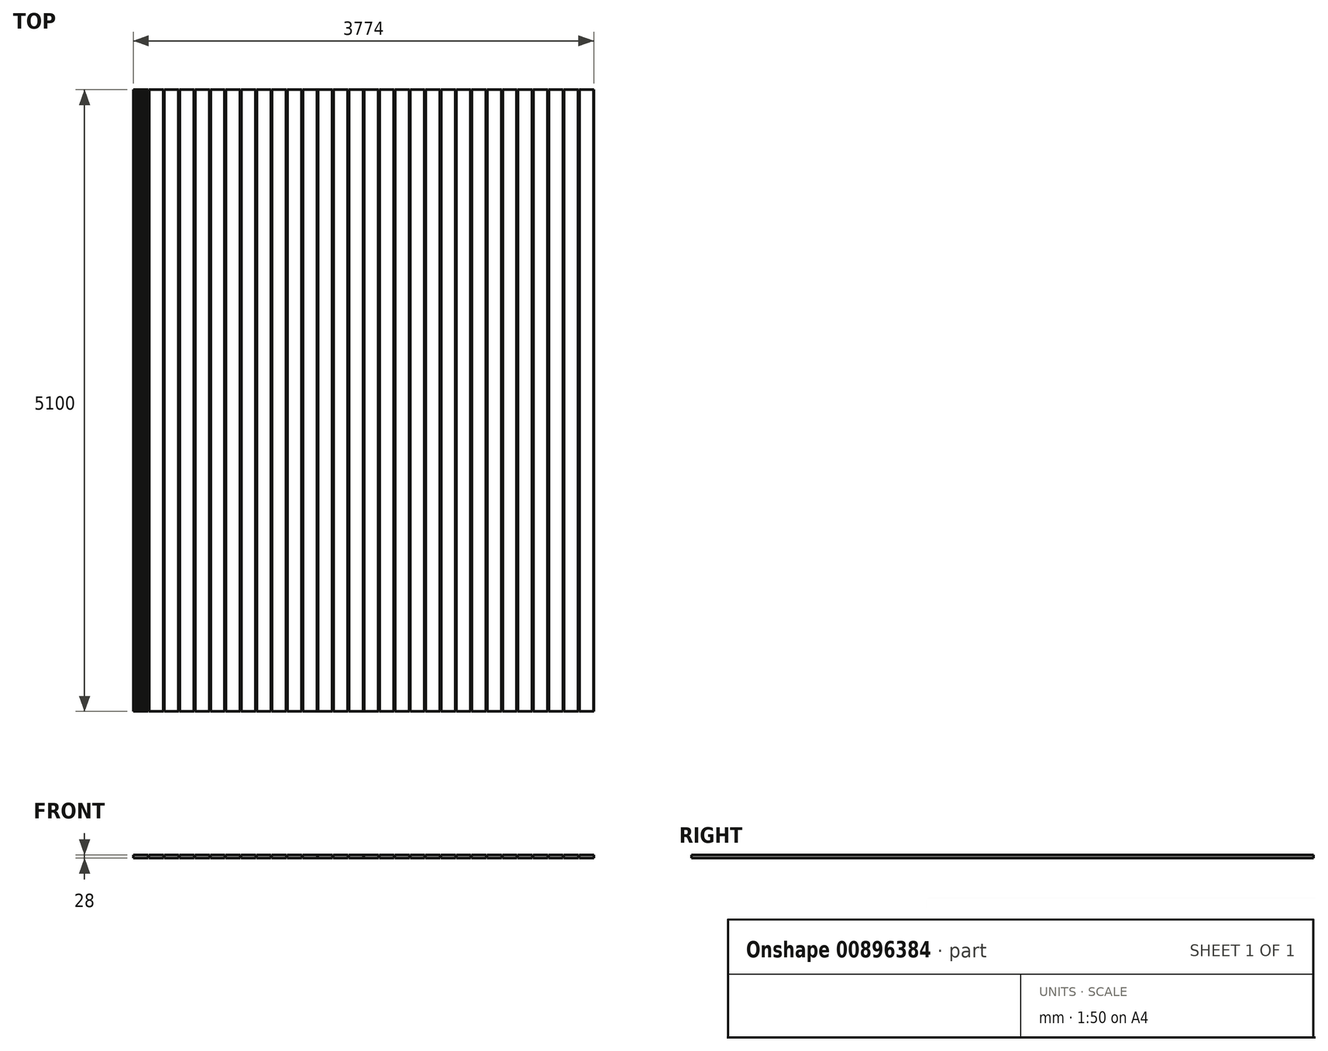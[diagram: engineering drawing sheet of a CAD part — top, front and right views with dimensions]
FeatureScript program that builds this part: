
annotation { "Feature Type Name" : "Feature", "Feature Type Description" : "" }
export const myFeature = defineFeature(function(context is Context, id is Id, definition is map)
    precondition{}
    {
        {
            var Q0;
            Q0=qCreatedBy(makeId("Top.planeOp"),FACE);
            var sketch = newSketch(context, id + "F0", { "sketchPlane" : qUnion([Q0])});
            skLineSegment(sketch, "E0.bottom", {"start": v(-61.1, -252.6) * mm, "end": v(58.9, -252.6) * mm});
            skLineSegment(sketch, "E0.top", {"start": v(-61.1, 4847.4) * mm, "end": v(58.9, 4847.4) * mm});
            skLineSegment(sketch, "E0.left", {"start": v(-61.1, -252.6) * mm, "end": v(-61.1, 4847.4) * mm});
            skLineSegment(sketch, "E0.right", {"start": v(58.9, -252.6) * mm, "end": v(58.9, 4847.4) * mm});
            skLineSegment(sketch, "E1.bottom", {"start": v(64.9, -252.6) * mm, "end": v(184.9, -252.6) * mm});
            skLineSegment(sketch, "E1.top", {"start": v(64.9, 4847.4) * mm, "end": v(184.9, 4847.4) * mm});
            skLineSegment(sketch, "E1.left", {"start": v(64.9, -252.6) * mm, "end": v(64.9, 4847.4) * mm});
            skLineSegment(sketch, "E1.right", {"start": v(184.9, -252.6) * mm, "end": v(184.9, 4847.4) * mm});
            skLineSegment(sketch, "E2.bottom", {"start": v(190.9, -252.6) * mm, "end": v(310.9, -252.6) * mm});
            skLineSegment(sketch, "E2.top", {"start": v(190.9, 4847.4) * mm, "end": v(310.9, 4847.4) * mm});
            skLineSegment(sketch, "E2.left", {"start": v(190.9, -252.6) * mm, "end": v(190.9, 4847.4) * mm});
            skLineSegment(sketch, "E2.right", {"start": v(310.9, -252.6) * mm, "end": v(310.9, 4847.4) * mm});
            skLineSegment(sketch, "E3.bottom", {"start": v(316.9, -252.6) * mm, "end": v(436.9, -252.6) * mm});
            skLineSegment(sketch, "E3.top", {"start": v(316.9, 4847.4) * mm, "end": v(436.9, 4847.4) * mm});
            skLineSegment(sketch, "E3.left", {"start": v(316.9, -252.6) * mm, "end": v(316.9, 4847.4) * mm});
            skLineSegment(sketch, "E3.right", {"start": v(436.9, -252.6) * mm, "end": v(436.9, 4847.4) * mm});
            skLineSegment(sketch, "E4.bottom", {"start": v(442.9, -252.6) * mm, "end": v(562.9, -252.6) * mm});
            skLineSegment(sketch, "E4.top", {"start": v(442.9, 4847.4) * mm, "end": v(562.9, 4847.4) * mm});
            skLineSegment(sketch, "E4.left", {"start": v(442.9, -252.6) * mm, "end": v(442.9, 4847.4) * mm});
            skLineSegment(sketch, "E4.right", {"start": v(562.9, -252.6) * mm, "end": v(562.9, 4847.4) * mm});
            skLineSegment(sketch, "E5.bottom", {"start": v(568.9, -252.6) * mm, "end": v(688.9, -252.6) * mm});
            skLineSegment(sketch, "E5.top", {"start": v(568.9, 4847.4) * mm, "end": v(688.9, 4847.4) * mm});
            skLineSegment(sketch, "E5.left", {"start": v(568.9, -252.6) * mm, "end": v(568.9, 4847.4) * mm});
            skLineSegment(sketch, "E5.right", {"start": v(688.9, -252.6) * mm, "end": v(688.9, 4847.4) * mm});
            skLineSegment(sketch, "E6.bottom", {"start": v(694.9, -252.6) * mm, "end": v(814.9, -252.6) * mm});
            skLineSegment(sketch, "E6.top", {"start": v(694.9, 4847.4) * mm, "end": v(814.9, 4847.4) * mm});
            skLineSegment(sketch, "E6.left", {"start": v(694.9, -252.6) * mm, "end": v(694.9, 4847.4) * mm});
            skLineSegment(sketch, "E6.right", {"start": v(814.9, -252.6) * mm, "end": v(814.9, 4847.4) * mm});
            skLineSegment(sketch, "E7.bottom", {"start": v(820.9, -252.6) * mm, "end": v(940.9, -252.6) * mm});
            skLineSegment(sketch, "E7.top", {"start": v(820.9, 4847.4) * mm, "end": v(940.9, 4847.4) * mm});
            skLineSegment(sketch, "E7.left", {"start": v(820.9, -252.6) * mm, "end": v(820.9, 4847.4) * mm});
            skLineSegment(sketch, "E7.right", {"start": v(940.9, -252.6) * mm, "end": v(940.9, 4847.4) * mm});
            skLineSegment(sketch, "E8.bottom", {"start": v(946.9, -252.6) * mm, "end": v(1066.9, -252.6) * mm});
            skLineSegment(sketch, "E8.top", {"start": v(946.9, 4847.4) * mm, "end": v(1066.9, 4847.4) * mm});
            skLineSegment(sketch, "E8.left", {"start": v(946.9, -252.6) * mm, "end": v(946.9, 4847.4) * mm});
            skLineSegment(sketch, "E8.right", {"start": v(1066.9, -252.6) * mm, "end": v(1066.9, 4847.4) * mm});
            skLineSegment(sketch, "E9.bottom", {"start": v(1072.9, -252.6) * mm, "end": v(1192.9, -252.6) * mm});
            skLineSegment(sketch, "E9.top", {"start": v(1072.9, 4847.4) * mm, "end": v(1192.9, 4847.4) * mm});
            skLineSegment(sketch, "E9.left", {"start": v(1072.9, -252.6) * mm, "end": v(1072.9, 4847.4) * mm});
            skLineSegment(sketch, "E9.right", {"start": v(1192.9, -252.6) * mm, "end": v(1192.9, 4847.4) * mm});
            skLineSegment(sketch, "E10.bottom", {"start": v(1198.9, -252.6) * mm, "end": v(1318.9, -252.6) * mm});
            skLineSegment(sketch, "E10.top", {"start": v(1198.9, 4847.4) * mm, "end": v(1318.9, 4847.4) * mm});
            skLineSegment(sketch, "E10.left", {"start": v(1198.9, -252.6) * mm, "end": v(1198.9, 4847.4) * mm});
            skLineSegment(sketch, "E10.right", {"start": v(1318.9, -252.6) * mm, "end": v(1318.9, 4847.4) * mm});
            skLineSegment(sketch, "E11.bottom", {"start": v(1324.9, -252.6) * mm, "end": v(1444.9, -252.6) * mm});
            skLineSegment(sketch, "E11.top", {"start": v(1324.9, 4847.4) * mm, "end": v(1444.9, 4847.4) * mm});
            skLineSegment(sketch, "E11.left", {"start": v(1324.9, -252.6) * mm, "end": v(1324.9, 4847.4) * mm});
            skLineSegment(sketch, "E11.right", {"start": v(1444.9, -252.6) * mm, "end": v(1444.9, 4847.4) * mm});
            skLineSegment(sketch, "E12.bottom", {"start": v(1450.9, -252.6) * mm, "end": v(1570.9, -252.6) * mm});
            skLineSegment(sketch, "E12.top", {"start": v(1450.9, 4847.4) * mm, "end": v(1570.9, 4847.4) * mm});
            skLineSegment(sketch, "E12.left", {"start": v(1450.9, -252.6) * mm, "end": v(1450.9, 4847.4) * mm});
            skLineSegment(sketch, "E12.right", {"start": v(1570.9, -252.6) * mm, "end": v(1570.9, 4847.4) * mm});
            skLineSegment(sketch, "E13.bottom", {"start": v(1576.9, -252.6) * mm, "end": v(1696.9, -252.6) * mm});
            skLineSegment(sketch, "E13.top", {"start": v(1576.9, 4847.4) * mm, "end": v(1696.9, 4847.4) * mm});
            skLineSegment(sketch, "E13.left", {"start": v(1576.9, -252.6) * mm, "end": v(1576.9, 4847.4) * mm});
            skLineSegment(sketch, "E13.right", {"start": v(1696.9, -252.6) * mm, "end": v(1696.9, 4847.4) * mm});
            skLineSegment(sketch, "E14.bottom", {"start": v(1702.9, -252.6) * mm, "end": v(1822.9, -252.6) * mm});
            skLineSegment(sketch, "E14.top", {"start": v(1702.9, 4847.4) * mm, "end": v(1822.9, 4847.4) * mm});
            skLineSegment(sketch, "E14.left", {"start": v(1702.9, -252.6) * mm, "end": v(1702.9, 4847.4) * mm});
            skLineSegment(sketch, "E14.right", {"start": v(1822.9, -252.6) * mm, "end": v(1822.9, 4847.4) * mm});
            skLineSegment(sketch, "E15.bottom", {"start": v(1828.9, -252.6) * mm, "end": v(1948.9, -252.6) * mm});
            skLineSegment(sketch, "E15.top", {"start": v(1828.9, 4847.4) * mm, "end": v(1948.9, 4847.4) * mm});
            skLineSegment(sketch, "E15.left", {"start": v(1828.9, -252.6) * mm, "end": v(1828.9, 4847.4) * mm});
            skLineSegment(sketch, "E15.right", {"start": v(1948.9, -252.6) * mm, "end": v(1948.9, 4847.4) * mm});
            skLineSegment(sketch, "E16.bottom", {"start": v(1954.9, -252.6) * mm, "end": v(2074.9, -252.6) * mm});
            skLineSegment(sketch, "E16.top", {"start": v(1954.9, 4847.4) * mm, "end": v(2074.9, 4847.4) * mm});
            skLineSegment(sketch, "E16.left", {"start": v(1954.9, -252.6) * mm, "end": v(1954.9, 4847.4) * mm});
            skLineSegment(sketch, "E16.right", {"start": v(2074.9, -252.6) * mm, "end": v(2074.9, 4847.4) * mm});
            skLineSegment(sketch, "E17.bottom", {"start": v(2080.9, -252.6) * mm, "end": v(2200.9, -252.6) * mm});
            skLineSegment(sketch, "E17.top", {"start": v(2080.9, 4847.4) * mm, "end": v(2200.9, 4847.4) * mm});
            skLineSegment(sketch, "E17.left", {"start": v(2080.9, -252.6) * mm, "end": v(2080.9, 4847.4) * mm});
            skLineSegment(sketch, "E17.right", {"start": v(2200.9, -252.6) * mm, "end": v(2200.9, 4847.4) * mm});
            skLineSegment(sketch, "E18.bottom", {"start": v(2206.9, -252.6) * mm, "end": v(2326.9, -252.6) * mm});
            skLineSegment(sketch, "E18.top", {"start": v(2206.9, 4847.4) * mm, "end": v(2326.9, 4847.4) * mm});
            skLineSegment(sketch, "E18.left", {"start": v(2206.9, -252.6) * mm, "end": v(2206.9, 4847.4) * mm});
            skLineSegment(sketch, "E18.right", {"start": v(2326.9, -252.6) * mm, "end": v(2326.9, 4847.4) * mm});
            skLineSegment(sketch, "E19.bottom", {"start": v(2332.9, -252.6) * mm, "end": v(2452.9, -252.6) * mm});
            skLineSegment(sketch, "E19.top", {"start": v(2332.9, 4847.4) * mm, "end": v(2452.9, 4847.4) * mm});
            skLineSegment(sketch, "E19.left", {"start": v(2332.9, -252.6) * mm, "end": v(2332.9, 4847.4) * mm});
            skLineSegment(sketch, "E19.right", {"start": v(2452.9, -252.6) * mm, "end": v(2452.9, 4847.4) * mm});
            skLineSegment(sketch, "E20.bottom", {"start": v(2458.9, -252.6) * mm, "end": v(2578.9, -252.6) * mm});
            skLineSegment(sketch, "E20.top", {"start": v(2458.9, 4847.4) * mm, "end": v(2578.9, 4847.4) * mm});
            skLineSegment(sketch, "E20.left", {"start": v(2458.9, -252.6) * mm, "end": v(2458.9, 4847.4) * mm});
            skLineSegment(sketch, "E20.right", {"start": v(2578.9, -252.6) * mm, "end": v(2578.9, 4847.4) * mm});
            skLineSegment(sketch, "E21.bottom", {"start": v(2584.9, -252.6) * mm, "end": v(2704.9, -252.6) * mm});
            skLineSegment(sketch, "E21.top", {"start": v(2584.9, 4847.4) * mm, "end": v(2704.9, 4847.4) * mm});
            skLineSegment(sketch, "E21.left", {"start": v(2584.9, -252.6) * mm, "end": v(2584.9, 4847.4) * mm});
            skLineSegment(sketch, "E21.right", {"start": v(2704.9, -252.6) * mm, "end": v(2704.9, 4847.4) * mm});
            skLineSegment(sketch, "E22.bottom", {"start": v(2710.9, -252.6) * mm, "end": v(2830.9, -252.6) * mm});
            skLineSegment(sketch, "E22.top", {"start": v(2710.9, 4847.4) * mm, "end": v(2830.9, 4847.4) * mm});
            skLineSegment(sketch, "E22.left", {"start": v(2710.9, -252.6) * mm, "end": v(2710.9, 4847.4) * mm});
            skLineSegment(sketch, "E22.right", {"start": v(2830.9, -252.6) * mm, "end": v(2830.9, 4847.4) * mm});
            skLineSegment(sketch, "E23.bottom", {"start": v(2836.9, -252.6) * mm, "end": v(2956.9, -252.6) * mm});
            skLineSegment(sketch, "E23.top", {"start": v(2836.9, 4847.4) * mm, "end": v(2956.9, 4847.4) * mm});
            skLineSegment(sketch, "E23.left", {"start": v(2836.9, -252.6) * mm, "end": v(2836.9, 4847.4) * mm});
            skLineSegment(sketch, "E23.right", {"start": v(2956.9, -252.6) * mm, "end": v(2956.9, 4847.4) * mm});
            skLineSegment(sketch, "E24.bottom", {"start": v(2962.9, -252.6) * mm, "end": v(3082.9, -252.6) * mm});
            skLineSegment(sketch, "E24.top", {"start": v(2962.9, 4847.4) * mm, "end": v(3082.9, 4847.4) * mm});
            skLineSegment(sketch, "E24.left", {"start": v(2962.9, -252.6) * mm, "end": v(2962.9, 4847.4) * mm});
            skLineSegment(sketch, "E24.right", {"start": v(3082.9, -252.6) * mm, "end": v(3082.9, 4847.4) * mm});
            skLineSegment(sketch, "E25.bottom", {"start": v(3088.9, -252.6) * mm, "end": v(3208.9, -252.6) * mm});
            skLineSegment(sketch, "E25.top", {"start": v(3088.9, 4847.4) * mm, "end": v(3208.9, 4847.4) * mm});
            skLineSegment(sketch, "E25.left", {"start": v(3088.9, -252.6) * mm, "end": v(3088.9, 4847.4) * mm});
            skLineSegment(sketch, "E25.right", {"start": v(3208.9, -252.6) * mm, "end": v(3208.9, 4847.4) * mm});
            skLineSegment(sketch, "E26.bottom", {"start": v(3214.9, -252.6) * mm, "end": v(3334.9, -252.6) * mm});
            skLineSegment(sketch, "E26.top", {"start": v(3214.9, 4847.4) * mm, "end": v(3334.9, 4847.4) * mm});
            skLineSegment(sketch, "E26.left", {"start": v(3214.9, -252.6) * mm, "end": v(3214.9, 4847.4) * mm});
            skLineSegment(sketch, "E26.right", {"start": v(3334.9, -252.6) * mm, "end": v(3334.9, 4847.4) * mm});
            skLineSegment(sketch, "E27.bottom", {"start": v(3340.9, -252.6) * mm, "end": v(3460.9, -252.6) * mm});
            skLineSegment(sketch, "E27.top", {"start": v(3340.9, 4847.4) * mm, "end": v(3460.9, 4847.4) * mm});
            skLineSegment(sketch, "E27.left", {"start": v(3340.9, -252.6) * mm, "end": v(3340.9, 4847.4) * mm});
            skLineSegment(sketch, "E27.right", {"start": v(3460.9, -252.6) * mm, "end": v(3460.9, 4847.4) * mm});
            skLineSegment(sketch, "E28.bottom", {"start": v(3466.9, -252.6) * mm, "end": v(3586.9, -252.6) * mm});
            skLineSegment(sketch, "E28.top", {"start": v(3466.9, 4847.4) * mm, "end": v(3586.9, 4847.4) * mm});
            skLineSegment(sketch, "E28.left", {"start": v(3466.9, -252.6) * mm, "end": v(3466.9, 4847.4) * mm});
            skLineSegment(sketch, "E28.right", {"start": v(3586.9, -252.6) * mm, "end": v(3586.9, 4847.4) * mm});
            skLineSegment(sketch, "E29.bottom", {"start": v(3592.9, -252.6) * mm, "end": v(3712.9, -252.6) * mm});
            skLineSegment(sketch, "E29.top", {"start": v(3592.9, 4847.4) * mm, "end": v(3712.9, 4847.4) * mm});
            skLineSegment(sketch, "E29.left", {"start": v(3592.9, -252.6) * mm, "end": v(3592.9, 4847.4) * mm});
            skLineSegment(sketch, "E29.right", {"start": v(3712.9, -252.6) * mm, "end": v(3712.9, 4847.4) * mm});
            skSolve(sketch);
        }
        {
            var Q0;
            Q0=makeQuery(id+"F0.imprint","IMPRINT",FACE,{"disambiguationData":[TD([[makeQuery(id+"F0.imprint","IMPRINT",EDGE,{"derivedFrom":sQuery(id+"F0.wireOp",EDGE,"E0.bottom")}),1.0]])]});
            var Q1;
            Q1=makeQuery(id+"F0.imprint","IMPRINT",FACE,{"disambiguationData":[TD([[makeQuery(id+"F0.imprint","IMPRINT",EDGE,{"derivedFrom":sQuery(id+"F0.wireOp",EDGE,"E18.bottom")}),1.0]])]});
            var Q2;
            Q2=makeQuery(id+"F0.imprint","IMPRINT",FACE,{"disambiguationData":[TD([[makeQuery(id+"F0.imprint","IMPRINT",EDGE,{"derivedFrom":sQuery(id+"F0.wireOp",EDGE,"E3.bottom")}),1.0]])]});
            var Q3;
            Q3=makeQuery(id+"F0.imprint","IMPRINT",FACE,{"disambiguationData":[TD([[makeQuery(id+"F0.imprint","IMPRINT",EDGE,{"derivedFrom":sQuery(id+"F0.wireOp",EDGE,"E17.bottom")}),1.0]])]});
            var Q4;
            Q4=makeQuery(id+"F0.imprint","IMPRINT",FACE,{"disambiguationData":[TD([[makeQuery(id+"F0.imprint","IMPRINT",EDGE,{"derivedFrom":sQuery(id+"F0.wireOp",EDGE,"E7.bottom")}),1.0]])]});
            var Q5;
            Q5=makeQuery(id+"F0.imprint","IMPRINT",FACE,{"disambiguationData":[TD([[makeQuery(id+"F0.imprint","IMPRINT",EDGE,{"derivedFrom":sQuery(id+"F0.wireOp",EDGE,"E13.bottom")}),1.0]])]});
            var Q6;
            Q6=makeQuery(id+"F0.imprint","IMPRINT",FACE,{"disambiguationData":[TD([[makeQuery(id+"F0.imprint","IMPRINT",EDGE,{"derivedFrom":sQuery(id+"F0.wireOp",EDGE,"E8.bottom")}),1.0]])]});
            var Q7;
            Q7=makeQuery(id+"F0.imprint","IMPRINT",FACE,{"disambiguationData":[TD([[makeQuery(id+"F0.imprint","IMPRINT",EDGE,{"derivedFrom":sQuery(id+"F0.wireOp",EDGE,"E22.bottom")}),1.0]])]});
            var Q8;
            Q8=makeQuery(id+"F0.imprint","IMPRINT",FACE,{"disambiguationData":[TD([[makeQuery(id+"F0.imprint","IMPRINT",EDGE,{"derivedFrom":sQuery(id+"F0.wireOp",EDGE,"E16.bottom")}),1.0]])]});
            var Q9;
            Q9=makeQuery(id+"F0.imprint","IMPRINT",FACE,{"disambiguationData":[TD([[makeQuery(id+"F0.imprint","IMPRINT",EDGE,{"derivedFrom":sQuery(id+"F0.wireOp",EDGE,"E9.bottom")}),1.0]])]});
            var Q10;
            Q10=makeQuery(id+"F0.imprint","IMPRINT",FACE,{"disambiguationData":[TD([[makeQuery(id+"F0.imprint","IMPRINT",EDGE,{"derivedFrom":sQuery(id+"F0.wireOp",EDGE,"E5.bottom")}),1.0]])]});
            var Q11;
            Q11=makeQuery(id+"F0.imprint","IMPRINT",FACE,{"disambiguationData":[TD([[makeQuery(id+"F0.imprint","IMPRINT",EDGE,{"derivedFrom":sQuery(id+"F0.wireOp",EDGE,"E6.bottom")}),1.0]])]});
            var Q12;
            Q12=makeQuery(id+"F0.imprint","IMPRINT",FACE,{"disambiguationData":[TD([[makeQuery(id+"F0.imprint","IMPRINT",EDGE,{"derivedFrom":sQuery(id+"F0.wireOp",EDGE,"E11.bottom")}),1.0]])]});
            var Q13;
            Q13=makeQuery(id+"F0.imprint","IMPRINT",FACE,{"disambiguationData":[TD([[makeQuery(id+"F0.imprint","IMPRINT",EDGE,{"derivedFrom":sQuery(id+"F0.wireOp",EDGE,"E10.bottom")}),1.0]])]});
            var Q14;
            Q14=makeQuery(id+"F0.imprint","IMPRINT",FACE,{"disambiguationData":[TD([[makeQuery(id+"F0.imprint","IMPRINT",EDGE,{"derivedFrom":sQuery(id+"F0.wireOp",EDGE,"E4.bottom")}),1.0]])]});
            var Q15;
            Q15=makeQuery(id+"F0.imprint","IMPRINT",FACE,{"disambiguationData":[TD([[makeQuery(id+"F0.imprint","IMPRINT",EDGE,{"derivedFrom":sQuery(id+"F0.wireOp",EDGE,"E24.bottom")}),1.0]])]});
            var Q16;
            Q16=makeQuery(id+"F0.imprint","IMPRINT",FACE,{"disambiguationData":[TD([[makeQuery(id+"F0.imprint","IMPRINT",EDGE,{"derivedFrom":sQuery(id+"F0.wireOp",EDGE,"E21.bottom")}),1.0]])]});
            var Q17;
            Q17=makeQuery(id+"F0.imprint","IMPRINT",FACE,{"disambiguationData":[TD([[makeQuery(id+"F0.imprint","IMPRINT",EDGE,{"derivedFrom":sQuery(id+"F0.wireOp",EDGE,"E12.bottom")}),1.0]])]});
            var Q18;
            Q18=makeQuery(id+"F0.imprint","IMPRINT",FACE,{"disambiguationData":[TD([[makeQuery(id+"F0.imprint","IMPRINT",EDGE,{"derivedFrom":sQuery(id+"F0.wireOp",EDGE,"E14.bottom")}),1.0]])]});
            var Q19;
            Q19=makeQuery(id+"F0.imprint","IMPRINT",FACE,{"disambiguationData":[TD([[makeQuery(id+"F0.imprint","IMPRINT",EDGE,{"derivedFrom":sQuery(id+"F0.wireOp",EDGE,"E23.bottom")}),1.0]])]});
            var Q20;
            Q20=makeQuery(id+"F0.imprint","IMPRINT",FACE,{"disambiguationData":[TD([[makeQuery(id+"F0.imprint","IMPRINT",EDGE,{"derivedFrom":sQuery(id+"F0.wireOp",EDGE,"E20.bottom")}),1.0]])]});
            var Q21;
            Q21=makeQuery(id+"F0.imprint","IMPRINT",FACE,{"disambiguationData":[TD([[makeQuery(id+"F0.imprint","IMPRINT",EDGE,{"derivedFrom":sQuery(id+"F0.wireOp",EDGE,"E19.bottom")}),1.0]])]});
            var Q22;
            Q22=makeQuery(id+"F0.imprint","IMPRINT",FACE,{"disambiguationData":[TD([[makeQuery(id+"F0.imprint","IMPRINT",EDGE,{"derivedFrom":sQuery(id+"F0.wireOp",EDGE,"E15.bottom")}),1.0]])]});
            var Q23;
            Q23=makeQuery(id+"F0.imprint","IMPRINT",FACE,{"disambiguationData":[TD([[makeQuery(id+"F0.imprint","IMPRINT",EDGE,{"derivedFrom":sQuery(id+"F0.wireOp",EDGE,"E1.bottom")}),1.0]])]});
            var Q24;
            Q24=makeQuery(id+"F0.imprint","IMPRINT",FACE,{"disambiguationData":[TD([[makeQuery(id+"F0.imprint","IMPRINT",EDGE,{"derivedFrom":sQuery(id+"F0.wireOp",EDGE,"E2.bottom")}),1.0]])]});
            var Q25;
            Q25=makeQuery(id+"F0.imprint","IMPRINT",FACE,{"disambiguationData":[TD([[makeQuery(id+"F0.imprint","IMPRINT",EDGE,{"derivedFrom":sQuery(id+"F0.wireOp",EDGE,"E25.bottom")}),1.0]])]});
            var Q26;
            Q26=makeQuery(id+"F0.imprint","IMPRINT",FACE,{"disambiguationData":[TD([[makeQuery(id+"F0.imprint","IMPRINT",EDGE,{"derivedFrom":sQuery(id+"F0.wireOp",EDGE,"E26.bottom")}),1.0]])]});
            var Q27;
            Q27=makeQuery(id+"F0.imprint","IMPRINT",FACE,{"disambiguationData":[TD([[makeQuery(id+"F0.imprint","IMPRINT",EDGE,{"derivedFrom":sQuery(id+"F0.wireOp",EDGE,"E27.bottom")}),1.0]])]});
            var Q28;
            Q28=makeQuery(id+"F0.imprint","IMPRINT",FACE,{"disambiguationData":[TD([[makeQuery(id+"F0.imprint","IMPRINT",EDGE,{"derivedFrom":sQuery(id+"F0.wireOp",EDGE,"E28.bottom")}),1.0]])]});
            var Q29;
            Q29=makeQuery(id+"F0.imprint","IMPRINT",FACE,{"disambiguationData":[TD([[makeQuery(id+"F0.imprint","IMPRINT",EDGE,{"derivedFrom":sQuery(id+"F0.wireOp",EDGE,"E29.bottom")}),1.0]])]});
            extrude(context, id + "F1", {"entities" : qUnion([Q0, Q1, Q2, Q3, Q4, Q5, Q6, Q7, Q8, Q9, Q10, Q11, Q12, Q13, Q14, Q15, Q16, Q17, Q18, Q19, Q20, Q21, Q22, Q23, Q24, Q25, Q26, Q27, Q28, Q29]), "depth" : 28 * mm, "offsetDistance" : 25 * mm});
        }
        {
            var Q0;
            Q0=makeQuery(id+"F1.opExtrude","CAP_EDGE",EDGE,{"disambiguationData":[OSD([sQuery(id+"F0.wireOp",EDGE,"E0.left")])],"isStart":false});
            var Q1;
            Q1=makeQuery(id+"F1.opExtrude","CAP_EDGE",EDGE,{"disambiguationData":[OSD([sQuery(id+"F0.wireOp",EDGE,"E0.right")])],"isStart":false});
            var Q2;
            Q2=makeQuery(id+"F1.opExtrude","CAP_EDGE",EDGE,{"disambiguationData":[OSD([sQuery(id+"F0.wireOp",EDGE,"E1.left")])],"isStart":false});
            var Q3;
            Q3=makeQuery(id+"F1.opExtrude","CAP_EDGE",EDGE,{"disambiguationData":[OSD([sQuery(id+"F0.wireOp",EDGE,"E1.right")])],"isStart":false});
            var Q4;
            Q4=makeQuery(id+"F1.opExtrude","CAP_EDGE",EDGE,{"disambiguationData":[OSD([sQuery(id+"F0.wireOp",EDGE,"E2.left")])],"isStart":false});
            var Q5;
            Q5=makeQuery(id+"F1.opExtrude","CAP_EDGE",EDGE,{"disambiguationData":[OSD([sQuery(id+"F0.wireOp",EDGE,"E2.right")])],"isStart":false});
            var Q6;
            Q6=makeQuery(id+"F1.opExtrude","CAP_EDGE",EDGE,{"disambiguationData":[OSD([sQuery(id+"F0.wireOp",EDGE,"E3.left")])],"isStart":false});
            var Q7;
            Q7=makeQuery(id+"F1.opExtrude","CAP_EDGE",EDGE,{"disambiguationData":[OSD([sQuery(id+"F0.wireOp",EDGE,"E3.right")])],"isStart":false});
            var Q8;
            Q8=makeQuery(id+"F1.opExtrude","CAP_EDGE",EDGE,{"disambiguationData":[OSD([sQuery(id+"F0.wireOp",EDGE,"E4.left")])],"isStart":false});
            var Q9;
            Q9=makeQuery(id+"F1.opExtrude","CAP_EDGE",EDGE,{"disambiguationData":[OSD([sQuery(id+"F0.wireOp",EDGE,"E4.right")])],"isStart":false});
            var Q10;
            Q10=makeQuery(id+"F1.opExtrude","CAP_EDGE",EDGE,{"disambiguationData":[OSD([sQuery(id+"F0.wireOp",EDGE,"E5.left")])],"isStart":false});
            var Q11;
            Q11=makeQuery(id+"F1.opExtrude","CAP_EDGE",EDGE,{"disambiguationData":[OSD([sQuery(id+"F0.wireOp",EDGE,"E5.right")])],"isStart":false});
            var Q12;
            Q12=makeQuery(id+"F1.opExtrude","CAP_EDGE",EDGE,{"disambiguationData":[OSD([sQuery(id+"F0.wireOp",EDGE,"E6.left")])],"isStart":false});
            var Q13;
            Q13=makeQuery(id+"F1.opExtrude","CAP_EDGE",EDGE,{"disambiguationData":[OSD([sQuery(id+"F0.wireOp",EDGE,"E6.right")])],"isStart":false});
            var Q14;
            Q14=makeQuery(id+"F1.opExtrude","CAP_EDGE",EDGE,{"disambiguationData":[OSD([sQuery(id+"F0.wireOp",EDGE,"E7.left")])],"isStart":false});
            var Q15;
            Q15=makeQuery(id+"F1.opExtrude","CAP_EDGE",EDGE,{"disambiguationData":[OSD([sQuery(id+"F0.wireOp",EDGE,"E8.left")])],"isStart":false});
            var Q16;
            Q16=makeQuery(id+"F1.opExtrude","CAP_EDGE",EDGE,{"disambiguationData":[OSD([sQuery(id+"F0.wireOp",EDGE,"E7.right")])],"isStart":false});
            var Q17;
            Q17=makeQuery(id+"F1.opExtrude","CAP_EDGE",EDGE,{"disambiguationData":[OSD([sQuery(id+"F0.wireOp",EDGE,"E8.right")])],"isStart":false});
            var Q18;
            Q18=makeQuery(id+"F1.opExtrude","CAP_EDGE",EDGE,{"disambiguationData":[OSD([sQuery(id+"F0.wireOp",EDGE,"E9.left")])],"isStart":false});
            var Q19;
            Q19=makeQuery(id+"F1.opExtrude","CAP_EDGE",EDGE,{"disambiguationData":[OSD([sQuery(id+"F0.wireOp",EDGE,"E9.right")])],"isStart":false});
            var Q20;
            Q20=makeQuery(id+"F1.opExtrude","CAP_EDGE",EDGE,{"disambiguationData":[OSD([sQuery(id+"F0.wireOp",EDGE,"E10.left")])],"isStart":false});
            var Q21;
            Q21=makeQuery(id+"F1.opExtrude","CAP_EDGE",EDGE,{"disambiguationData":[OSD([sQuery(id+"F0.wireOp",EDGE,"E10.right")])],"isStart":false});
            var Q22;
            Q22=makeQuery(id+"F1.opExtrude","CAP_EDGE",EDGE,{"disambiguationData":[OSD([sQuery(id+"F0.wireOp",EDGE,"E11.left")])],"isStart":false});
            var Q23;
            Q23=makeQuery(id+"F1.opExtrude","CAP_EDGE",EDGE,{"disambiguationData":[OSD([sQuery(id+"F0.wireOp",EDGE,"E11.right")])],"isStart":false});
            var Q24;
            Q24=makeQuery(id+"F1.opExtrude","CAP_EDGE",EDGE,{"disambiguationData":[OSD([sQuery(id+"F0.wireOp",EDGE,"E12.left")])],"isStart":false});
            var Q25;
            Q25=makeQuery(id+"F1.opExtrude","CAP_EDGE",EDGE,{"disambiguationData":[OSD([sQuery(id+"F0.wireOp",EDGE,"E12.right")])],"isStart":false});
            var Q26;
            Q26=makeQuery(id+"F1.opExtrude","CAP_EDGE",EDGE,{"disambiguationData":[OSD([sQuery(id+"F0.wireOp",EDGE,"E13.left")])],"isStart":false});
            var Q27;
            Q27=makeQuery(id+"F1.opExtrude","CAP_EDGE",EDGE,{"disambiguationData":[OSD([sQuery(id+"F0.wireOp",EDGE,"E13.right")])],"isStart":false});
            var Q28;
            Q28=makeQuery(id+"F1.opExtrude","CAP_EDGE",EDGE,{"disambiguationData":[OSD([sQuery(id+"F0.wireOp",EDGE,"E14.left")])],"isStart":false});
            var Q29;
            Q29=makeQuery(id+"F1.opExtrude","CAP_EDGE",EDGE,{"disambiguationData":[OSD([sQuery(id+"F0.wireOp",EDGE,"E14.right")])],"isStart":false});
            var Q30;
            Q30=makeQuery(id+"F1.opExtrude","CAP_EDGE",EDGE,{"disambiguationData":[OSD([sQuery(id+"F0.wireOp",EDGE,"E15.left")])],"isStart":false});
            var Q31;
            Q31=makeQuery(id+"F1.opExtrude","CAP_EDGE",EDGE,{"disambiguationData":[OSD([sQuery(id+"F0.wireOp",EDGE,"E15.right")])],"isStart":false});
            var Q32;
            Q32=makeQuery(id+"F1.opExtrude","CAP_EDGE",EDGE,{"disambiguationData":[OSD([sQuery(id+"F0.wireOp",EDGE,"E16.left")])],"isStart":false});
            var Q33;
            Q33=makeQuery(id+"F1.opExtrude","CAP_EDGE",EDGE,{"disambiguationData":[OSD([sQuery(id+"F0.wireOp",EDGE,"E16.right")])],"isStart":false});
            var Q34;
            Q34=makeQuery(id+"F1.opExtrude","CAP_EDGE",EDGE,{"disambiguationData":[OSD([sQuery(id+"F0.wireOp",EDGE,"E17.left")])],"isStart":false});
            var Q35;
            Q35=makeQuery(id+"F1.opExtrude","CAP_EDGE",EDGE,{"disambiguationData":[OSD([sQuery(id+"F0.wireOp",EDGE,"E17.right")])],"isStart":false});
            var Q36;
            Q36=makeQuery(id+"F1.opExtrude","CAP_EDGE",EDGE,{"disambiguationData":[OSD([sQuery(id+"F0.wireOp",EDGE,"E18.left")])],"isStart":false});
            var Q37;
            Q37=makeQuery(id+"F1.opExtrude","CAP_EDGE",EDGE,{"disambiguationData":[OSD([sQuery(id+"F0.wireOp",EDGE,"E18.right")])],"isStart":false});
            var Q38;
            Q38=makeQuery(id+"F1.opExtrude","CAP_EDGE",EDGE,{"disambiguationData":[OSD([sQuery(id+"F0.wireOp",EDGE,"E19.left")])],"isStart":false});
            var Q39;
            Q39=makeQuery(id+"F1.opExtrude","CAP_EDGE",EDGE,{"disambiguationData":[OSD([sQuery(id+"F0.wireOp",EDGE,"E19.right")])],"isStart":false});
            var Q40;
            Q40=makeQuery(id+"F1.opExtrude","CAP_EDGE",EDGE,{"disambiguationData":[OSD([sQuery(id+"F0.wireOp",EDGE,"E20.left")])],"isStart":false});
            var Q41;
            Q41=makeQuery(id+"F1.opExtrude","CAP_EDGE",EDGE,{"disambiguationData":[OSD([sQuery(id+"F0.wireOp",EDGE,"E20.right")])],"isStart":false});
            var Q42;
            Q42=makeQuery(id+"F1.opExtrude","CAP_EDGE",EDGE,{"disambiguationData":[OSD([sQuery(id+"F0.wireOp",EDGE,"E21.left")])],"isStart":false});
            var Q43;
            Q43=makeQuery(id+"F1.opExtrude","CAP_EDGE",EDGE,{"disambiguationData":[OSD([sQuery(id+"F0.wireOp",EDGE,"E21.right")])],"isStart":false});
            var Q44;
            Q44=makeQuery(id+"F1.opExtrude","CAP_EDGE",EDGE,{"disambiguationData":[OSD([sQuery(id+"F0.wireOp",EDGE,"E22.left")])],"isStart":false});
            var Q45;
            Q45=makeQuery(id+"F1.opExtrude","CAP_EDGE",EDGE,{"disambiguationData":[OSD([sQuery(id+"F0.wireOp",EDGE,"E22.right")])],"isStart":false});
            var Q46;
            Q46=makeQuery(id+"F1.opExtrude","CAP_EDGE",EDGE,{"disambiguationData":[OSD([sQuery(id+"F0.wireOp",EDGE,"E23.left")])],"isStart":false});
            var Q47;
            Q47=makeQuery(id+"F1.opExtrude","CAP_EDGE",EDGE,{"disambiguationData":[OSD([sQuery(id+"F0.wireOp",EDGE,"E23.right")])],"isStart":false});
            var Q48;
            Q48=makeQuery(id+"F1.opExtrude","CAP_EDGE",EDGE,{"disambiguationData":[OSD([sQuery(id+"F0.wireOp",EDGE,"E24.left")])],"isStart":false});
            var Q49;
            Q49=makeQuery(id+"F1.opExtrude","CAP_EDGE",EDGE,{"disambiguationData":[OSD([sQuery(id+"F0.wireOp",EDGE,"E24.right")])],"isStart":false});
            var Q50;
            Q50=makeQuery(id+"F1.opExtrude","CAP_EDGE",EDGE,{"disambiguationData":[OSD([sQuery(id+"F0.wireOp",EDGE,"E25.left")])],"isStart":false});
            var Q51;
            Q51=makeQuery(id+"F1.opExtrude","CAP_EDGE",EDGE,{"disambiguationData":[OSD([sQuery(id+"F0.wireOp",EDGE,"E26.left")])],"isStart":false});
            var Q52;
            Q52=makeQuery(id+"F1.opExtrude","CAP_EDGE",EDGE,{"disambiguationData":[OSD([sQuery(id+"F0.wireOp",EDGE,"E25.right")])],"isStart":false});
            var Q53;
            Q53=makeQuery(id+"F1.opExtrude","CAP_EDGE",EDGE,{"disambiguationData":[OSD([sQuery(id+"F0.wireOp",EDGE,"E26.right")])],"isStart":false});
            var Q54;
            Q54=makeQuery(id+"F1.opExtrude","CAP_EDGE",EDGE,{"disambiguationData":[OSD([sQuery(id+"F0.wireOp",EDGE,"E27.left")])],"isStart":false});
            var Q55;
            Q55=makeQuery(id+"F1.opExtrude","CAP_EDGE",EDGE,{"disambiguationData":[OSD([sQuery(id+"F0.wireOp",EDGE,"E28.left")])],"isStart":false});
            var Q56;
            Q56=makeQuery(id+"F1.opExtrude","CAP_EDGE",EDGE,{"disambiguationData":[OSD([sQuery(id+"F0.wireOp",EDGE,"E27.right")])],"isStart":false});
            var Q57;
            Q57=makeQuery(id+"F1.opExtrude","CAP_EDGE",EDGE,{"disambiguationData":[OSD([sQuery(id+"F0.wireOp",EDGE,"E29.left")])],"isStart":false});
            var Q58;
            Q58=makeQuery(id+"F1.opExtrude","CAP_EDGE",EDGE,{"disambiguationData":[OSD([sQuery(id+"F0.wireOp",EDGE,"E28.right")])],"isStart":false});
            var Q59;
            Q59=makeQuery(id+"F1.opExtrude","CAP_EDGE",EDGE,{"disambiguationData":[OSD([sQuery(id+"F0.wireOp",EDGE,"E29.right")])],"isStart":false});
            chamfer(context, id + "F2", {"entities" : qUnion([Q0, Q1, Q2, Q3, Q4, Q5, Q6, Q7, Q8, Q9, Q10, Q11, Q12, Q13, Q14, Q15, Q16, Q17, Q18, Q19, Q20, Q21, Q22, Q23, Q24, Q25, Q26, Q27, Q28, Q29, Q30, Q31, Q32, Q33, Q34, Q35, Q36, Q37, Q38, Q39, Q40, Q41, Q42, Q43, Q44, Q45, Q46, Q47, Q48, Q49, Q50, Q51, Q52, Q53, Q54, Q55, Q56, Q57, Q58, Q59]), "width" : 3 * mm, "tangentPropagation" : true});
        }
        {
            var Q0;
            Q0=makeQuery(id+"F1.opExtrude","SWEPT_FACE",FACE,{"disambiguationData":[OSD([sQuery(id+"F0.wireOp",EDGE,"E0.bottom")])]});
            var sketch = newSketch(context, id + "F3", { "sketchPlane" : qUnion([Q0])});
            skLineSegment(sketch, "E30", {"start": v(-60.94, 0) * mm, "end": v(-60.94, 25) * mm});
            skLineSegment(sketch, "E31", {"start": v(-60.94, 25) * mm, "end": v(-57.94, 28) * mm});
            skLineSegment(sketch, "E32", {"start": v(-57.94, 28) * mm, "end": v(-47.94, 28) * mm});
            skLineSegment(sketch, "E33", {"start": v(-44.94, 25) * mm, "end": v(-47.94, 28) * mm});
            skLineSegment(sketch, "E34", {"start": v(-44.94, 25) * mm, "end": v(-39.94, 25) * mm});
            skLineSegment(sketch, "E35", {"start": v(-39.94, 25) * mm, "end": v(-36.94, 28) * mm});
            skLineSegment(sketch, "E36", {"start": v(-36.94, 28) * mm, "end": v(-26.94, 28) * mm});
            skLineSegment(sketch, "E37", {"start": v(-26.94, 28) * mm, "end": v(-23.94, 25) * mm});
            skLineSegment(sketch, "E38", {"start": v(-23.94, 25) * mm, "end": v(-19.94, 25) * mm});
            skLineSegment(sketch, "E39", {"start": v(-16.94, 28) * mm, "end": v(-19.94, 25) * mm});
            skLineSegment(sketch, "E40", {"start": v(-16.94, 28) * mm, "end": v(-6.94, 28) * mm});
            skLineSegment(sketch, "E41", {"start": v(-6.94, 28) * mm, "end": v(-3.94, 25) * mm});
            skLineSegment(sketch, "E42", {"start": v(-3.94, 25) * mm, "end": v(1.06, 25) * mm});
            skLineSegment(sketch, "E43", {"start": v(4.06, 28) * mm, "end": v(1.06, 25) * mm});
            skLineSegment(sketch, "E44", {"start": v(4.06, 28) * mm, "end": v(14.06, 28) * mm});
            skLineSegment(sketch, "E45", {"start": v(14.06, 28) * mm, "end": v(17.06, 25) * mm});
            skLineSegment(sketch, "E46", {"start": v(17.06, 25) * mm, "end": v(22.06, 25) * mm});
            skLineSegment(sketch, "E47", {"start": v(25.06, 28) * mm, "end": v(22.06, 25) * mm});
            skLineSegment(sketch, "E48", {"start": v(25.06, 28) * mm, "end": v(35.06, 28) * mm});
            skLineSegment(sketch, "E49", {"start": v(35.06, 28) * mm, "end": v(38.06, 25) * mm});
            skLineSegment(sketch, "E50", {"start": v(38.06, 25) * mm, "end": v(43.06, 25) * mm});
            skLineSegment(sketch, "E51", {"start": v(46.06, 28) * mm, "end": v(43.06, 25) * mm});
            skLineSegment(sketch, "E52", {"start": v(46.06, 28) * mm, "end": v(56.06, 28) * mm});
            skLineSegment(sketch, "E53", {"start": v(56.06, 28) * mm, "end": v(59.06, 25) * mm});
            skLineSegment(sketch, "E54", {"start": v(59.06, 25) * mm, "end": v(59.06, 0) * mm});
            skLineSegment(sketch, "E55", {"start": v(59.06, 0) * mm, "end": v(-60.94, 0) * mm});
            skLineSegment(sketch, "E56", {"start": v(-47.94, 28) * mm, "end": v(-36.94, 28) * mm});
            skLineSegment(sketch, "E57", {"start": v(-26.94, 28) * mm, "end": v(-16.94, 28) * mm});
            skLineSegment(sketch, "E58", {"start": v(-6.94, 28) * mm, "end": v(4.06, 28) * mm});
            skLineSegment(sketch, "E59", {"start": v(14.06, 28) * mm, "end": v(25.06, 28) * mm});
            skLineSegment(sketch, "E60", {"start": v(35.06, 28) * mm, "end": v(46.06, 28) * mm});
            skSolve(sketch);
        }
        {
            var Q0;
            Q0=makeQuery(id+"F3.imprint","IMPRINT",FACE,{"disambiguationData":[TD([[makeQuery(id+"F3.imprint","IMPRINT",EDGE,{"derivedFrom":sQuery(id+"F3.wireOp",EDGE,"E33")}),-1.0]])]});
            var Q1;
            Q1=makeQuery(id+"F3.imprint","IMPRINT",FACE,{"disambiguationData":[TD([[makeQuery(id+"F3.imprint","IMPRINT",EDGE,{"derivedFrom":sQuery(id+"F3.wireOp",EDGE,"E37")}),1.0]])]});
            var Q2;
            Q2=makeQuery(id+"F3.imprint","IMPRINT",FACE,{"disambiguationData":[TD([[makeQuery(id+"F3.imprint","IMPRINT",EDGE,{"derivedFrom":sQuery(id+"F3.wireOp",EDGE,"E41")}),1.0]])]});
            var Q3;
            Q3=makeQuery(id+"F3.imprint","IMPRINT",FACE,{"disambiguationData":[TD([[makeQuery(id+"F3.imprint","IMPRINT",EDGE,{"derivedFrom":sQuery(id+"F3.wireOp",EDGE,"E45")}),1.0]])]});
            var Q4;
            Q4=makeQuery(id+"F3.imprint","IMPRINT",FACE,{"disambiguationData":[TD([[makeQuery(id+"F3.imprint","IMPRINT",EDGE,{"derivedFrom":sQuery(id+"F3.wireOp",EDGE,"E49")}),1.0]])]});
            extrude(context, id + "F4", {"entities" : qUnion([Q0, Q1, Q2, Q3, Q4]), "operationType" : NewBodyOperationType.REMOVE, "oppositeDirection" : true, "depth" : 5100 * mm, "offsetDistance" : 25 * mm});
        }
    });
